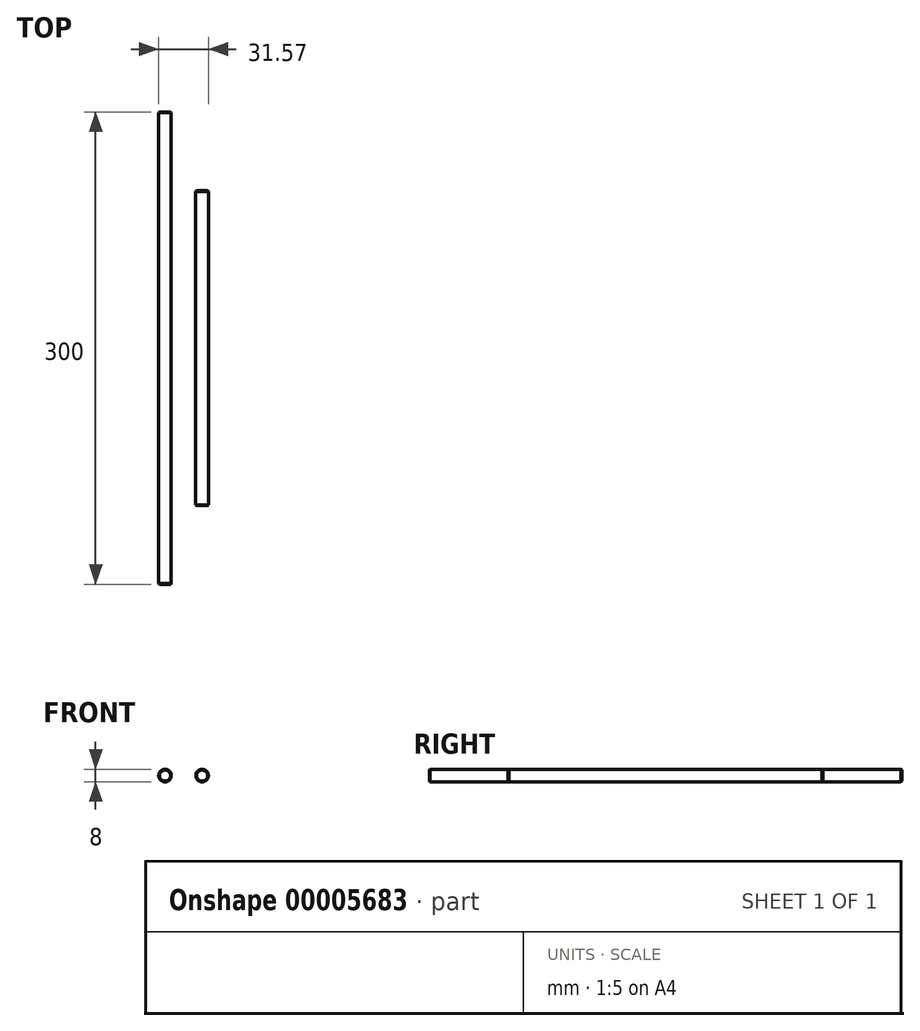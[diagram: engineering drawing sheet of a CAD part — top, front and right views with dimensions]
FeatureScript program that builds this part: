
annotation { "Feature Type Name" : "Feature", "Feature Type Description" : "" }
export const myFeature = defineFeature(function(context is Context, id is Id, definition is map)
    precondition{}
    {
        {
            var Q0;
            Q0=qCreatedBy(makeId("Front.planeOp"),FACE);
            var sketch = newSketch(context, id + "F0", { "sketchPlane" : qUnion([Q0])});
            skCircle(sketch, "E0", {"center": v(0, 0) * mm, "radius": 4 * mm});
            skSolve(sketch);
        }
        {
            var Q0;
            Q0=makeQuery(id+"F0.imprint","IMPRINT",FACE,{"disambiguationData":[TD([[makeQuery(id+"F0.imprint","IMPRINT",EDGE,{"derivedFrom":sQuery(id+"F0.wireOp",EDGE,"E0")}),1.0]])]});
            extrude(context, id + "F1", {"entities" : qUnion([Q0]), "depth" : 300 * mm, "symmetric" : true});
        }
        {
            var Q0;
            Q0=makeQuery(id+"F1.opExtrude","SWEPT_FACE",FACE,{"disambiguationData":[OSD([sQuery(id+"F0.wireOp",EDGE,"E0")])]});
            chamfer(context, id + "F2", {"entities" : qUnion([Q0]), "width" : .5 * mm, "tangentPropagation" : true});
        }
        {
            var Q0;
            Q0=qCreatedBy(makeId("Front.planeOp"),FACE);
            var sketch = newSketch(context, id + "F3", { "sketchPlane" : qUnion([Q0])});
            skCircle(sketch, "E1", {"center": v(23.57, 0) * mm, "radius": 4 * mm});
            skSolve(sketch);
        }
        {
            var Q0;
            Q0=makeQuery(id+"F3.imprint","IMPRINT",FACE,{"disambiguationData":[TD([[makeQuery(id+"F3.imprint","IMPRINT",EDGE,{"derivedFrom":sQuery(id+"F3.wireOp",EDGE,"E1")}),1.0]])]});
            extrude(context, id + "F4", {"entities" : qUnion([Q0]), "depth" : 200 * mm, "symmetric" : true});
        }
        {
            var Q0;
            Q0=makeQuery(id+"F4.opExtrude","SWEPT_FACE",FACE,{"disambiguationData":[OSD([sQuery(id+"F3.wireOp",EDGE,"E1")])]});
            chamfer(context, id + "F5", {"entities" : qUnion([Q0]), "width" : .5 * mm, "tangentPropagation" : true});
        }
    });
